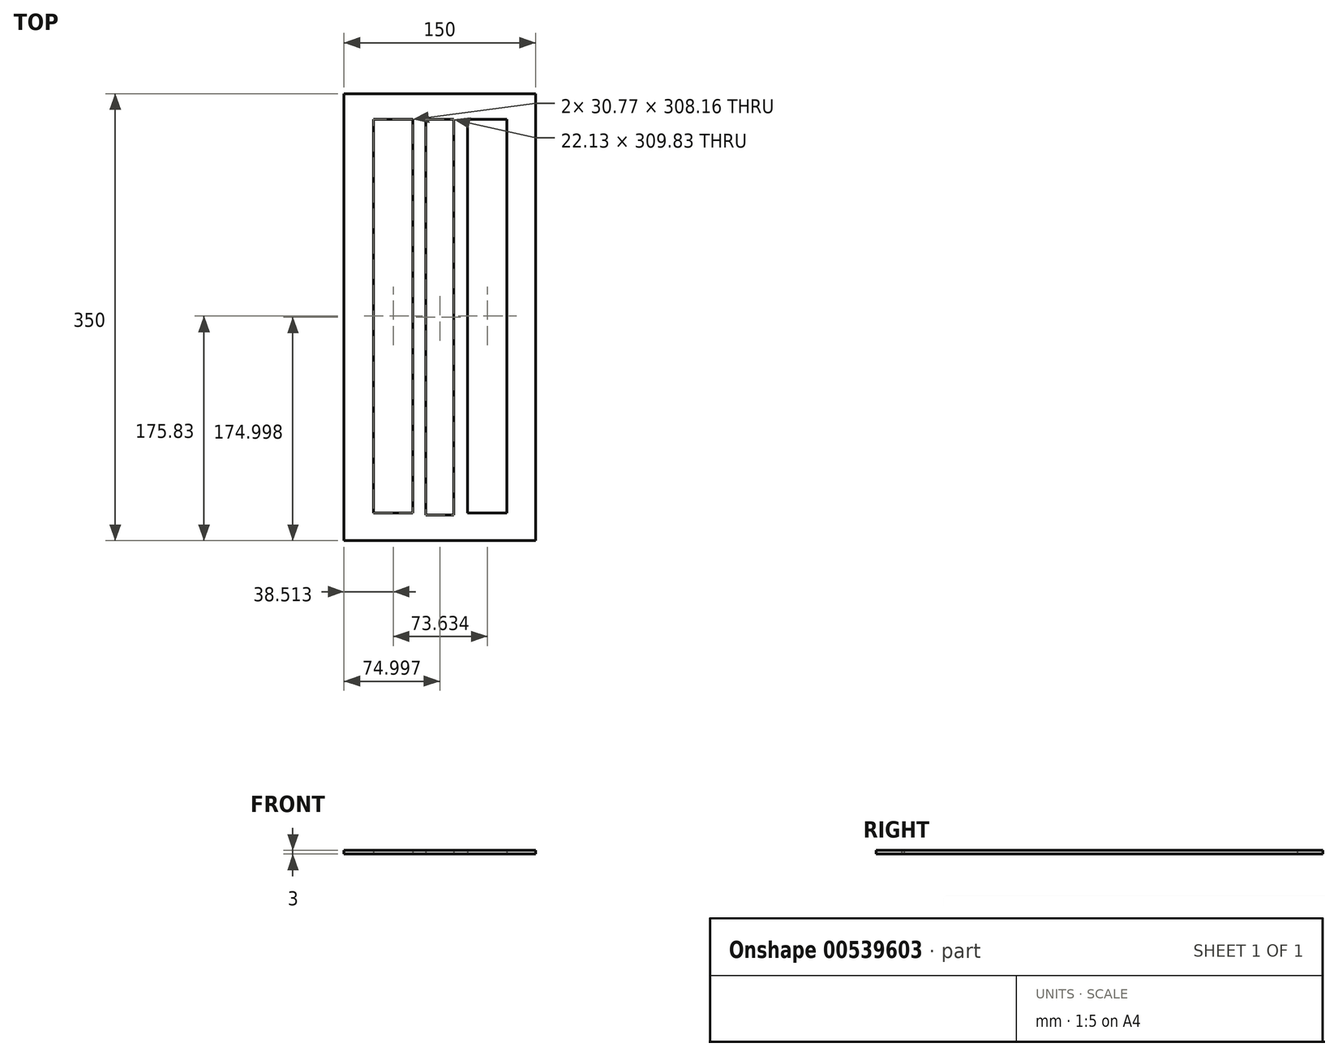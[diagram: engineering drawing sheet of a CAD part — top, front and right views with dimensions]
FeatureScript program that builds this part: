
annotation { "Feature Type Name" : "Feature", "Feature Type Description" : "" }
export const myFeature = defineFeature(function(context is Context, id is Id, definition is map)
    precondition{}
    {
        {
            var Q0;
            Q0=qCreatedBy(makeId("Top.planeOp"),FACE);
            var sketch = newSketch(context, id + "F0", { "sketchPlane" : qUnion([Q0])});
            skLineSegment(sketch, "E0.bottom", {"start": v(-75.33, 174.17) * mm, "end": v(74.67, 174.17) * mm});
            skLineSegment(sketch, "E0.top", {"start": v(-75.33, -175.83) * mm, "end": v(74.67, -175.83) * mm});
            skLineSegment(sketch, "E0.left", {"start": v(-75.33, 174.17) * mm, "end": v(-75.33, -175.83) * mm});
            skLineSegment(sketch, "E0.right", {"start": v(74.67, 174.17) * mm, "end": v(74.67, -175.83) * mm});
            skPoint(sketch, "E0.middle", {"position": v(-0.33, -0.83) * mm});
            skLineSegment(sketch, "E1.bottom", {"start": v(21.43, 154.08) * mm, "end": v(52.2, 154.08) * mm});
            skLineSegment(sketch, "E1.top", {"start": v(21.43, -154.08) * mm, "end": v(52.2, -154.08) * mm});
            skLineSegment(sketch, "E1.left", {"start": v(21.43, 154.08) * mm, "end": v(21.43, -154.08) * mm});
            skLineSegment(sketch, "E1.right", {"start": v(52.2, 154.08) * mm, "end": v(52.2, -154.08) * mm});
            skPoint(sketch, "E1.middle", {"position": v(36.82, 0) * mm});
            skLineSegment(sketch, "E2", {"start": v(0, 226.32) * mm, "end": v(0, -195.08) * mm, "construction": true});
            skLineSegment(sketch, "E3.MirrorCS", {"start": v(-21.43, 154.08) * mm, "end": v(-21.43, -154.08) * mm});
            skLineSegment(sketch, "E4.MirrorCS", {"start": v(-52.2, 154.08) * mm, "end": v(-52.2, -154.08) * mm});
            skLineSegment(sketch, "E5.MirrorCS", {"start": v(-21.43, 154.08) * mm, "end": v(-52.2, 154.08) * mm});
            skLineSegment(sketch, "E6.MirrorCS", {"start": v(-21.43, -154.08) * mm, "end": v(-52.2, -154.08) * mm});
            skLineSegment(sketch, "E7.bottom", {"start": v(10.73, 154.08) * mm, "end": v(-11.4, 154.08) * mm});
            skLineSegment(sketch, "E7.top", {"start": v(10.73, -155.75) * mm, "end": v(-11.4, -155.75) * mm});
            skLineSegment(sketch, "E7.left", {"start": v(10.73, 154.08) * mm, "end": v(10.73, -155.75) * mm});
            skLineSegment(sketch, "E7.right", {"start": v(-11.4, 154.08) * mm, "end": v(-11.4, -155.75) * mm});
            skSolve(sketch);
        }
        {
            var Q0;
            Q0=makeQuery(id+"F0.imprint","IMPRINT",FACE,{"disambiguationData":[TD([[makeQuery(id+"F0.imprint","IMPRINT",EDGE,{"derivedFrom":sQuery(id+"F0.wireOp",EDGE,"E0.bottom")}),-1.0]])]});
            extrude(context, id + "F1", {"entities" : qUnion([Q0]), "depth" : 3 * mm, "offsetDistance" : 25 * mm});
        }
    });
